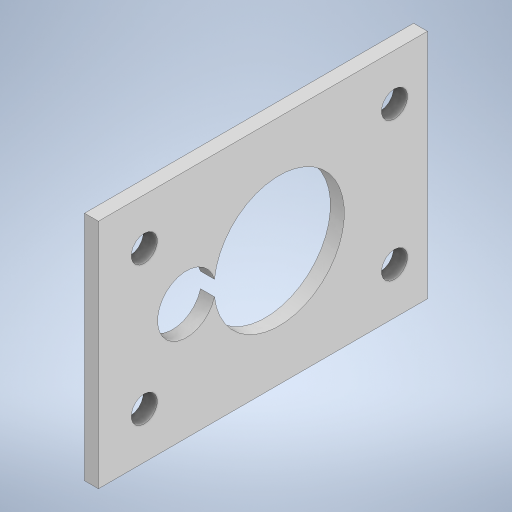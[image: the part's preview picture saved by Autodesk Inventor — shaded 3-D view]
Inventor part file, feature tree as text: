
AUTODESK INVENTOR PART (.ipt)
format: ipt  version: 2023 (Build 270158000, 158)  size: 235,520 bytes
history: native  units: in
note: dims shown in document units (in); Inventor stores cm internally (conversion verified against a paired STEP export)
features: extrude x1, sketch x1
ambient origin geometry x8: Origin, YZ Plane, XZ Plane, XY Plane, X Axis, Y Axis, Z Axis, Center Point
bodies: Solid1 (feature_tree)
feature tree (2):
  extrude  "Extrusion1"  Depth=0.71in
  sketch  "Sketch1"  dims[d0=0.5in d1=0.71in d2=0.75in d3=0.125in d5=0.0563in d9=0.54in d10=0.3in d11=0.3in d12=0.54in d13=0.1in d18=0.03in d19=0.0in d20=0.2812in d21=0.125in]
